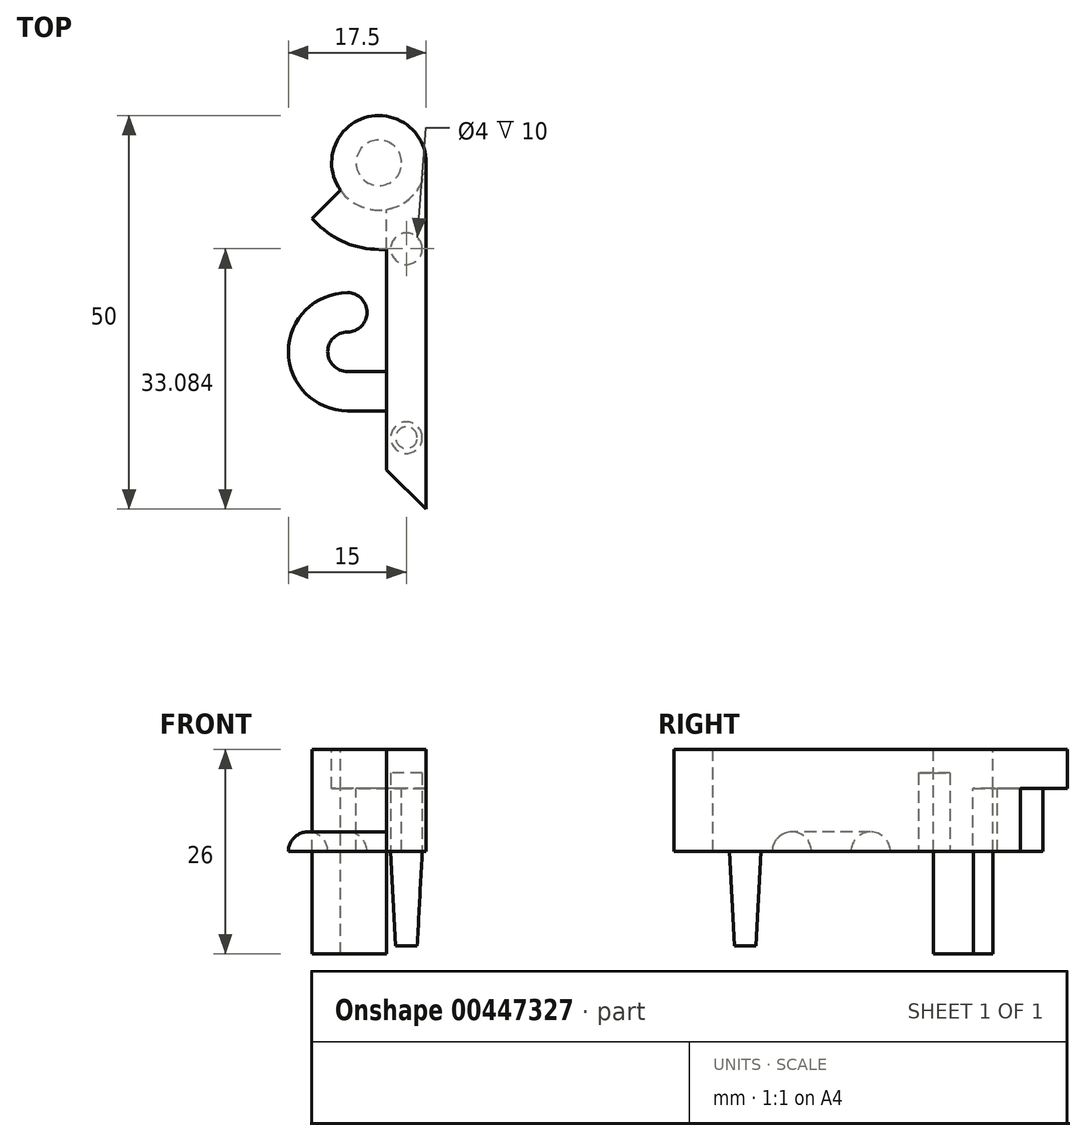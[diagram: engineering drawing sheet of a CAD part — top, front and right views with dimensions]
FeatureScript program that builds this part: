
annotation { "Feature Type Name" : "Feature", "Feature Type Description" : "" }
export const myFeature = defineFeature(function(context is Context, id is Id, definition is map)
    precondition{}
    {
        {
            var Q0;
            Q0=qCreatedBy(makeId("Top.planeOp"),FACE);
            var sketch = newSketch(context, id + "F0", { "sketchPlane" : qUnion([Q0])});
            skArc(sketch, "E0", {"start": v(6, 0) * mm, "mid": v(-4.58, 3.87) * mm, "end": v(1, -5.92) * mm});
            skLineSegment(sketch, "E1", {"start": v(6, 0) * mm, "end": v(6, -44) * mm});
            skLineSegment(sketch, "E2", {"start": v(6, -44) * mm, "end": v(1, -39) * mm});
            skLineSegment(sketch, "E3", {"start": v(1, -39) * mm, "end": v(1, -5.92) * mm});
            skLineSegment(sketch, "E4", {"start": v(0, 6) * mm, "end": v(41.48, 6) * mm, "construction": true});
            skSolve(sketch);
        }
        {
            var Q0;
            Q0=qSketchRegion(id+"F0",true);
            extrude(context, id + "F1", {"entities" : qUnion([Q0]), "depth" : 5 * mm});
        }
        {
            var Q0;
            Q0=makeQuery(id+"F1.opExtrude","CAP_FACE",FACE,{"disambiguationData":[OSD([sQuery(id+"F0.wireOp",EDGE,"E0"),sQuery(id+"F0.wireOp",EDGE,"E1"),sQuery(id+"F0.wireOp",EDGE,"E2"),sQuery(id+"F0.wireOp",EDGE,"E3")])],"isStart":false});
            var sketch = newSketch(context, id + "F2", { "sketchPlane" : qUnion([Q0])});
            skArc(sketch, "E5", {"start": v(1, -5.92) * mm, "mid": v(4.58, -3.87) * mm, "end": v(6, 0) * mm});
            skLineSegment(sketch, "E6", {"start": v(1, -5.92) * mm, "end": v(1, -39) * mm});
            skLineSegment(sketch, "E7", {"start": v(1, -39) * mm, "end": v(6, -44) * mm});
            skLineSegment(sketch, "E8", {"start": v(6, -44) * mm, "end": v(6, 0) * mm});
            skSolve(sketch);
        }
        {
            var Q0;
            Q0=qSketchRegion(id+"F2",true);
            extrude(context, id + "F3", {"entities" : qUnion([Q0]), "operationType" : NewBodyOperationType.ADD, "depth" : 8 * mm});
        }
        {
            var Q0;
            Q0=makeQuery(id+"F3.opExtrude","CAP_FACE",FACE,{"disambiguationData":[OSD([sQuery(id+"F2.wireOp",EDGE,"E5"),sQuery(id+"F2.wireOp",EDGE,"E6"),sQuery(id+"F2.wireOp",EDGE,"E7"),sQuery(id+"F2.wireOp",EDGE,"E8")])],"isStart":false});
            var sketch = newSketch(context, id + "F4", { "sketchPlane" : qUnion([Q0])});
            skCircle(sketch, "E9", {"center": v(3.5, -10.92) * mm, "radius": 2 * mm});
            skLineSegment(sketch, "E10", {"start": v(3.5, -10.92) * mm, "end": v(3.5, -30.92) * mm, "construction": true});
            skSolve(sketch);
        }
        {
            var Q0;
            Q0=qSketchRegion(id+"F4",true);
            extrude(context, id + "F5", {"entities" : qUnion([Q0]), "operationType" : NewBodyOperationType.REMOVE, "oppositeDirection" : true, "depth" : 10 * mm});
        }
        {
            var Q0;
            Q0=makeQuery(id+"F3.opExtrude","CAP_FACE",FACE,{"disambiguationData":[OSD([sQuery(id+"F2.wireOp",EDGE,"E5"),sQuery(id+"F2.wireOp",EDGE,"E6"),sQuery(id+"F2.wireOp",EDGE,"E7"),sQuery(id+"F2.wireOp",EDGE,"E8")])],"isStart":false});
            var sketch = newSketch(context, id + "F6", { "sketchPlane" : qUnion([Q0])});
            skCircle(sketch, "E11", {"center": v(3.5, -34.92) * mm, "radius": 2 * mm});
            skLineSegment(sketch, "E12", {"start": v(3.5, -34.92) * mm, "end": v(3.5, -18.91) * mm, "construction": true});
            skSolve(sketch);
        }
        {
            var Q0;
            Q0=qSketchRegion(id+"F6",true);
            extrude(context, id + "F7", {"entities" : qUnion([Q0]), "operationType" : NewBodyOperationType.ADD, "depth" : 12 * mm, "hasDraft" : true, "draftAngle" : 3 * degree, "draftPullDirection" : true});
        }
        {
            var Q0;
            Q0=makeQuery(id+"F1.opExtrude","CAP_FACE",FACE,{"disambiguationData":[OSD([sQuery(id+"F0.wireOp",EDGE,"E0"),sQuery(id+"F0.wireOp",EDGE,"E1"),sQuery(id+"F0.wireOp",EDGE,"E2"),sQuery(id+"F0.wireOp",EDGE,"E3")])],"isStart":false});
            var sketch = newSketch(context, id + "F8", { "sketchPlane" : qUnion([Q0])});
            skCircle(sketch, "E13", {"center": v(0, 0) * mm, "radius": 2.9 * mm});
            skSolve(sketch);
        }
        {
            var Q0;
            Q0=qSketchRegion(id+"F8",true);
            var Q1;
            Q1=makeQuery(id+"F3.opExtrude","CAP_FACE",FACE,{"disambiguationData":[OSD([sQuery(id+"F2.wireOp",EDGE,"E5"),sQuery(id+"F2.wireOp",EDGE,"E6"),sQuery(id+"F2.wireOp",EDGE,"E7"),sQuery(id+"F2.wireOp",EDGE,"E8")])],"isStart":false});
            extrude(context, id + "F9", {"entities" : qUnion([Q0]), "operationType" : NewBodyOperationType.ADD, "endBound" : BoundingType.UP_TO_SURFACE, "endBoundEntityFace" : qUnion([Q1]), "depth" : 25 * mm});
        }
        {
            var Q0;
            Q0=makeQuery(id+"F1.opExtrude","SWEPT_BODY",BODY,{"disambiguationData":[OSD([sQuery(id+"F0.wireOp",EDGE,"E0"),sQuery(id+"F0.wireOp",EDGE,"E1"),sQuery(id+"F0.wireOp",EDGE,"E2"),sQuery(id+"F0.wireOp",EDGE,"E3")])]});
            var Q1;
            Q1=makeQuery(id+"F3.opExtrude","CAP_FACE",FACE,{"disambiguationData":[OSD([sQuery(id+"F2.wireOp",EDGE,"E5"),sQuery(id+"F2.wireOp",EDGE,"E6"),sQuery(id+"F2.wireOp",EDGE,"E7"),sQuery(id+"F2.wireOp",EDGE,"E8")])],"isStart":false});
            mirror(context, id + "F10", {"entities" : qUnion([Q0]), "mirrorPlane" : qUnion([Q1])});
        }
        {
            var Q0;
            Q0=makeQuery(id+"F1.opExtrude","SWEPT_BODY",BODY,{"disambiguationData":[OSD([sQuery(id+"F0.wireOp",EDGE,"E0"),sQuery(id+"F0.wireOp",EDGE,"E1"),sQuery(id+"F0.wireOp",EDGE,"E2"),sQuery(id+"F0.wireOp",EDGE,"E3")])]});
            deleteBodies(context, id + "F11", {"entities" : qUnion([Q0])});
        }
        {
            var Q0;
            Q0=makeQuery(id+"F10.opPattern","COPY",FACE,{"derivedFrom":makeQuery(id+"F3.opExtrude","CAP_FACE",FACE,{"disambiguationData":[OSD([sQuery(id+"F2.wireOp",EDGE,"E5"),sQuery(id+"F2.wireOp",EDGE,"E6"),sQuery(id+"F2.wireOp",EDGE,"E7"),sQuery(id+"F2.wireOp",EDGE,"E8")])],"isStart":false}),"instanceName":"1"});
            var sketch = newSketch(context, id + "F12", { "sketchPlane" : qUnion([Q0])});
            skLineSegment(sketch, "E14", {"start": v(1, 29) * mm, "end": v(-4, 29) * mm});
            skArc(sketch, "E15", {"start": v(-4, 29) * mm, "mid": v(-9, 24) * mm, "end": v(-4, 19) * mm});
            skSolve(sketch);
        }
        {
            var Q0;
            Q0=makeQuery(id+"F10.opPattern","COPY",FACE,{"derivedFrom":makeQuery(id+"F3.boolean.opBoolean","MERGE",FACE,{"derivedFrom":[makeQuery(id+"F1.opExtrude","SWEPT_FACE",FACE,{"disambiguationData":[OSD([sQuery(id+"F0.wireOp",EDGE,"E3")])]}),makeQuery(id+"F3.opExtrude","SWEPT_FACE",FACE,{"disambiguationData":[OSD([sQuery(id+"F2.wireOp",EDGE,"E6")])]})]}),"instanceName":"1"});
            var sketch = newSketch(context, id + "F13", { "sketchPlane" : qUnion([Q0])});
            skArc(sketch, "E16", {"start": v(26.5, 13) * mm, "mid": v(29, 15.5) * mm, "end": v(31.5, 13) * mm});
            skLineSegment(sketch, "E17", {"start": v(26.5, 13) * mm, "end": v(31.5, 13) * mm});
            skSolve(sketch);
        }
        {
            var Q0;
            Q0 = qSketchRegion(id + "F13", true);
            var Q1;
            Q1 = qConstructionFilter(qBodyType(qCreatedBy(id + "F12" ,EDGE), BodyType.WIRE), ConstructionObject.NO);
            sweep(context, id + "F14", {"operationType" : NewBodyOperationType.ADD, "profiles" : qUnion([Q0]), "path" : qUnion([Q1])});
        }
        {
            var Q0;
            Q0=makeQuery(id+"F14.opSweep","CAP_FACE",FACE,{"disambiguationData":[OSD([sQuery(id+"F12.wireOp",VERTEX,"E15.end"),sQuery(id+"F13.wireOp",EDGE,"E16"),sQuery(id+"F13.wireOp",EDGE,"E17")])],"isStart":false});
            var sketch = newSketch(context, id + "F15", { "sketchPlane" : qUnion([Q0])});
            skArc(sketch, "E18", {"start": v(-16.5, 13) * mm, "mid": v(-17.23, 14.77) * mm, "end": v(-19, 15.5) * mm});
            skLineSegment(sketch, "E19", {"start": v(-19, 13) * mm, "end": v(-19, 15.5) * mm});
            skLineSegment(sketch, "E20", {"start": v(-19, 13) * mm, "end": v(-16.5, 13) * mm});
            skSolve(sketch);
        }
        {
            var Q0;
            Q0 = qSketchRegion(id + "F15", true);
            var Q1;
            Q1=sQuery(id+"F15.wireOp",EDGE,"E19");
            revolve(context, id + "F16", {"operationType" : NewBodyOperationType.ADD, "entities" : qUnion([Q0]), "axis" : qUnion([Q1]), "revolveType" : RevolveType.FULL});
        }
        {
            var Q0;
            Q0=makeQuery(id+"F10.opPattern","COPY",FACE,{"derivedFrom":makeQuery(id+"F1.opExtrude","CAP_FACE",FACE,{"disambiguationData":[OSD([sQuery(id+"F0.wireOp",EDGE,"E0"),sQuery(id+"F0.wireOp",EDGE,"E1"),sQuery(id+"F0.wireOp",EDGE,"E2"),sQuery(id+"F0.wireOp",EDGE,"E3")])],"isStart":true}),"instanceName":"1"});
            var sketch = newSketch(context, id + "F17", { "sketchPlane" : qUnion([Q0])});
            skLineSegment(sketch, "E21", {"start": v(-4.24, -4.24) * mm, "end": v(-7.78, -7.78) * mm, "construction": true});
            skArc(sketch, "E22", {"start": v(-7.78, -7.78) * mm, "mid": v(-4.2, -10.16) * mm, "end": v(0, -11) * mm});
            skLineSegment(sketch, "E23", {"start": v(0, -11) * mm, "end": v(1, -11) * mm});
            skLineSegment(sketch, "E24", {"start": v(1, -11) * mm, "end": v(1, -5.92) * mm});
            skArc(sketch, "E25", {"start": v(-4.9, -3.48) * mm, "mid": v(-2.3, -5.54) * mm, "end": v(1, -5.92) * mm});
            skLineSegment(sketch, "E26", {"start": v(-7.78, -7.78) * mm, "end": v(-8.49, -7.07) * mm});
            skLineSegment(sketch, "E27", {"start": v(-8.49, -7.07) * mm, "end": v(-4.9, -3.48) * mm});
            skSolve(sketch);
        }
        {
            var Q0;
            Q0 = qSketchRegion(id + "F17", true);
            extrude(context, id + "F18", {"entities" : qUnion([Q0]), "operationType" : NewBodyOperationType.ADD, "oppositeDirection" : true, "depth" : 26 * mm});
        }
    });
